# Revit family: FU_Chair_Sandler_Kontea 3-1
name_source: partatom
category: Furniture
units: mm (PartAtom-declared; Revit-internal decimal feet)

## family parameters
Always vertical = Yes
Cut with Voids When Loaded = No
OmniClass Number = 23.40.20.00
OmniClass Title = General Furniture and Specialties
Room Calculation Point = No
Shared = No
Work Plane-Based = No

## types (1)
- Kontea 3.1
    Default Elevation = 0 mm  [stored 0 ft]
    Depth = 600 mm  [stored 1.9685 ft]
    Description = Barstool with upholstered seat and back on steel base. Base spread 50cm / 20″ diameter. 360° swivel without memory return.
    Height = 1180 mm  [stored 3.87139 ft]
    Manufacturer = Sandler
    Model = Kontea 3.1
    URL = https://www.sandlerseating.com
    Width = 580 mm  [stored 1.90289 ft]

note: [stored X ft] marks values corroborated as IEEE doubles in the binary element streams (Revit-internal decimal feet)

## geometry (parser evidence)
native form markers: Sweep x8
no freeform markers — native parametric forms only
